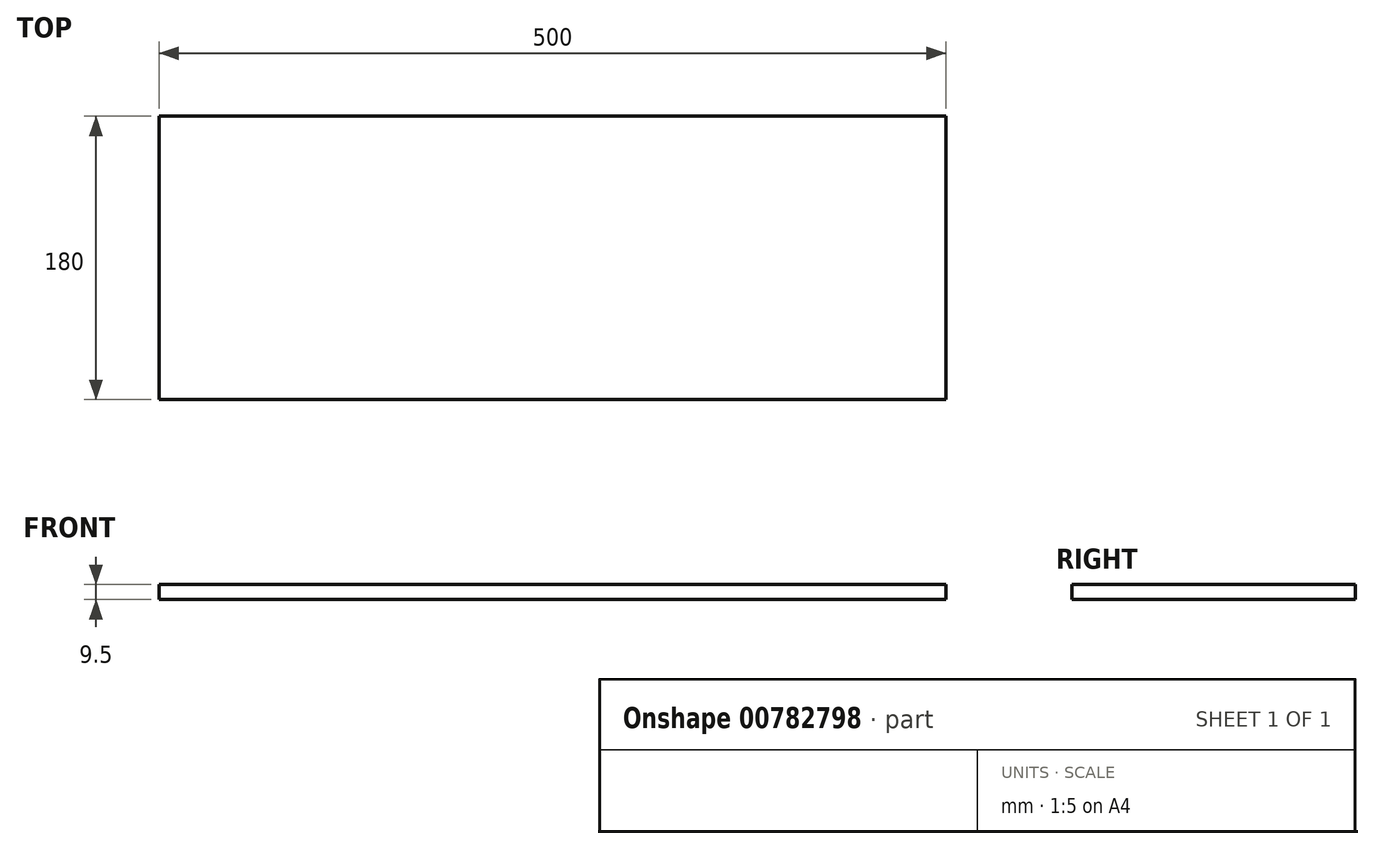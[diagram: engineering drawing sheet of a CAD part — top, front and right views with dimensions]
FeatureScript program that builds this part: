
annotation { "Feature Type Name" : "Feature", "Feature Type Description" : "" }
export const myFeature = defineFeature(function(context is Context, id is Id, definition is map)
    precondition{}
    {
        {
            var Q0;
            Q0=qCreatedBy(makeId("Top.planeOp"),FACE);
            var sketch = newSketch(context, id + "F0", { "sketchPlane" : qUnion([Q0])});
            skLineSegment(sketch, "E0.bottom", {"start": v(-32.6, -12.31) * mm, "end": v(467.4, -12.31) * mm});
            skLineSegment(sketch, "E0.top", {"start": v(-32.6, 167.69) * mm, "end": v(467.4, 167.69) * mm});
            skLineSegment(sketch, "E0.left", {"start": v(-32.6, -12.31) * mm, "end": v(-32.6, 167.69) * mm});
            skLineSegment(sketch, "E0.right", {"start": v(467.4, -12.31) * mm, "end": v(467.4, 167.69) * mm});
            skLineSegment(sketch, "E1", {"start": v(-32.6, -12.31) * mm, "end": v(-32.6, 17.69) * mm});
            skLineSegment(sketch, "E2", {"start": v(-32.6, 17.69) * mm, "end": v(467.4, 17.69) * mm});
            skLineSegment(sketch, "E3", {"start": v(-32.6, -12.31) * mm, "end": v(-32.6, 97.69) * mm});
            skLineSegment(sketch, "E4", {"start": v(467.4, 167.69) * mm, "end": v(467.4, 48.19) * mm});
            skLineSegment(sketch, "E5", {"start": v(467.4, 48.19) * mm, "end": v(-32.6, 48.19) * mm});
            skSolve(sketch);
        }
        {
            var Q0;
            Q0=makeQuery(id+"F0.imprint","IMPRINT",FACE,{"disambiguationData":[TD([[makeQuery(id+"F0.imprint","IMPRINT",EDGE,{"derivedFrom":sQuery(id+"F0.wireOp",EDGE,"E0.top")}),-1.0]])]});
            var Q1;
            {var subQ2=sQuery(id+"F0.wireOp",EDGE,"E2");Q1=makeQuery(id+"F0.imprint","IMPRINT",FACE,{"disambiguationData":[TD([[makeQuery(id+"F0.imprint","IMPRINT",EDGE,{"derivedFrom":subQ2}),1.0]])]});}
            var Q2;
            {var subQ0=sQuery(id+"F0.wireOp",EDGE,"E0.bottom");Q2=makeQuery(id+"F0.imprint","IMPRINT",FACE,{"disambiguationData":[TD([[makeQuery(id+"F0.imprint","IMPRINT",EDGE,{"derivedFrom":subQ0}),1.0]])]});}
            extrude(context, id + "F1", {"entities" : qUnion([Q0, Q1, Q2]), "depth" : 9.5 * mm, "offsetDistance" : 25 * mm});
        }
        {
            var Q0;
            Q0=makeQuery(id+"F1.opExtrude","CAP_FACE",FACE,{"disambiguationData":[OSD([sQuery(id+"F0.wireOp",EDGE,"E0.bottom"),sQuery(id+"F0.wireOp",EDGE,"E0.top"),sQuery(id+"F0.wireOp",EDGE,"E0.left"),sQuery(id+"F0.wireOp",EDGE,"E0.right")])],"isStart":true});
            var sketch = newSketch(context, id + "F2", { "sketchPlane" : qUnion([Q0])});
            skLineSegment(sketch, "E6", {"start": v(467.4, -137.69) * mm, "end": v(-32.6, -137.69) * mm});
            skLineSegment(sketch, "E7", {"start": v(-32.6, 12.31) * mm, "end": v(-32.6, -17.69) * mm});
            skLineSegment(sketch, "E8", {"start": v(-32.6, -17.69) * mm, "end": v(467.4, -17.69) * mm});
            skLineSegment(sketch, "E9", {"start": v(-32.6, -2.69) * mm, "end": v(467.4, -2.69) * mm});
            skLineSegment(sketch, "E10", {"start": v(-32.6, -167.69) * mm, "end": v(-32.6, -152.69) * mm});
            skLineSegment(sketch, "E11", {"start": v(-32.6, -152.69) * mm, "end": v(467.4, -152.69) * mm});
            skSolve(sketch);
        }
    });
